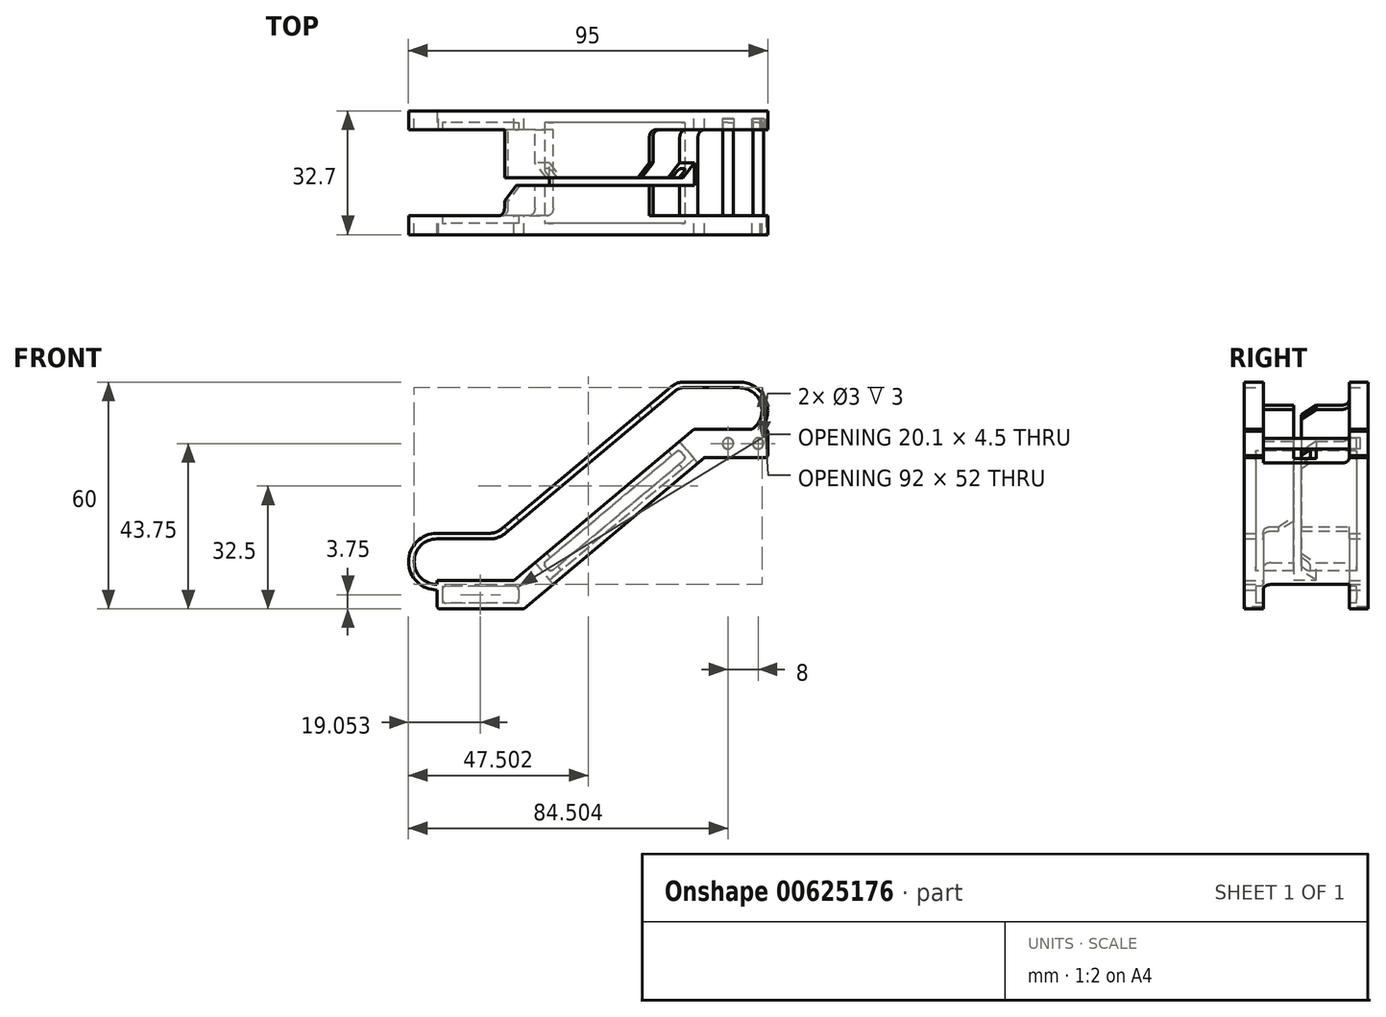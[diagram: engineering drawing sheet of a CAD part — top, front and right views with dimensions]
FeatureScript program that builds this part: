
annotation { "Feature Type Name" : "Feature", "Feature Type Description" : "" }
export const myFeature = defineFeature(function(context is Context, id is Id, definition is map)
    precondition{}
    {
        {
            var Q0;
            Q0=qCreatedBy(makeId("Front.planeOp"),FACE);
            var sketch = newSketch(context, id + "F0", { "sketchPlane" : qUnion([Q0])});
            skLineSegment(sketch, "E0", {"start": v(0, 0) * mm, "end": v(-32.65, 38.92) * mm, "construction": true});
            skLineSegment(sketch, "E1", {"start": v(-32.65, 38.92) * mm, "end": v(25.72, 87.9) * mm, "construction": true});
            skLineSegment(sketch, "E2", {"start": v(25.72, 87.9) * mm, "end": v(58.37, 48.98) * mm, "construction": true});
            skLineSegment(sketch, "E3", {"start": v(58.37, 48.98) * mm, "end": v(0, 0) * mm, "construction": true});
            skLineSegment(sketch, "E4", {"start": v(0, 0) * mm, "end": v(134.97, 0) * mm, "construction": true});
            skLineSegment(sketch, "E5.bottom", {"start": v(8.43, 66.15) * mm, "end": v(19.82, 66.15) * mm, "construction": true});
            skLineSegment(sketch, "E5.top", {"start": v(8.43, 20.9) * mm, "end": v(19.82, 20.9) * mm, "construction": true});
            skLineSegment(sketch, "E5.left", {"start": v(8.43, 66.15) * mm, "end": v(8.43, 20.9) * mm, "construction": true});
            skLineSegment(sketch, "E5.right", {"start": v(19.82, 66.15) * mm, "end": v(19.82, 20.9) * mm, "construction": true});
            skSolve(sketch);
        }
        {
            var Q0;
            Q0=qCreatedBy(makeId("Front.planeOp"),FACE);
            var sketch = newSketch(context, id + "F1", { "sketchPlane" : qUnion([Q0])});
            skLineSegment(sketch, "E6.0", {"start": v(0, 0) * mm, "end": v(134.97, 0) * mm, "construction": true});
            skLineSegment(sketch, "E7.0", {"start": v(58.37, 48.98) * mm, "end": v(0, 0) * mm, "construction": true});
            skLineSegment(sketch, "E8", {"start": v(2.16, 16.17) * mm, "end": v(47.04, 53.83) * mm});
            skLineSegment(sketch, "E9", {"start": v(-1.06, 15) * mm, "end": v(-15.06, 15) * mm});
            skLineSegment(sketch, "E10", {"start": v(50.25, 55) * mm, "end": v(64.94, 55) * mm});
            skLineSegment(sketch, "E11.0", {"start": v(55.71, 40) * mm, "end": v(64.94, 40) * mm});
            skLineSegment(sketch, "E11.1", {"start": v(7.62, 1.17) * mm, "end": v(52.5, 38.83) * mm});
            skLineSegment(sketch, "E11.2", {"start": v(4.4, 0) * mm, "end": v(-15.06, 0) * mm});
            skArc(sketch, "E12", {"start": v(-15.06, 15) * mm, "mid": v(-22.56, 7.5) * mm, "end": v(-15.06, 0) * mm});
            skArc(sketch, "E13", {"start": v(64.94, 55) * mm, "mid": v(72.44, 47.5) * mm, "end": v(64.94, 40) * mm});
            skLineSegment(sketch, "E14", {"start": v(-22.56, 7.5) * mm, "end": v(-22.56, 15.37) * mm, "construction": true});
            skLineSegment(sketch, "E15", {"start": v(72.44, 47.5) * mm, "end": v(72.44, 63.27) * mm, "construction": true});
            skPoint(sketch, "E16.visualSharp", {"position": v(0.76, 15) * mm});
            skArc(sketch, "E16.filletArc", {"start": v(-1.06, 15) * mm, "mid": v(0.65, 15.3) * mm, "end": v(2.16, 16.17) * mm});
            skPoint(sketch, "E17.visualSharp", {"position": v(6.22, 0) * mm});
            skArc(sketch, "E17.filletArc", {"start": v(4.4, 0) * mm, "mid": v(6.11, 0.3) * mm, "end": v(7.62, 1.17) * mm});
            skPoint(sketch, "E18.visualSharp", {"position": v(48.43, 55) * mm});
            skArc(sketch, "E18.filletArc", {"start": v(50.25, 55) * mm, "mid": v(48.54, 54.7) * mm, "end": v(47.04, 53.83) * mm});
            skPoint(sketch, "E19.visualSharp", {"position": v(53.9, 40) * mm});
            skArc(sketch, "E19.filletArc", {"start": v(55.71, 40) * mm, "mid": v(54, 39.7) * mm, "end": v(52.5, 38.83) * mm});
            skLineSegment(sketch, "E20.0", {"start": v(-1.06, 13.5) * mm, "end": v(-15.06, 13.5) * mm});
            skArc(sketch, "E20.1", {"start": v(55.71, 41.5) * mm, "mid": v(53.49, 41.1) * mm, "end": v(51.53, 39.98) * mm});
            skLineSegment(sketch, "E20.2", {"start": v(6.65, 2.32) * mm, "end": v(51.53, 39.98) * mm});
            skArc(sketch, "E20.3", {"start": v(4.4, 1.5) * mm, "mid": v(5.6, 1.71) * mm, "end": v(6.65, 2.32) * mm});
            skLineSegment(sketch, "E20.4", {"start": v(4.4, 1.5) * mm, "end": v(-15.06, 1.5) * mm});
            skLineSegment(sketch, "E20.5", {"start": v(55.71, 41.5) * mm, "end": v(64.94, 41.5) * mm});
            skArc(sketch, "E20.6", {"start": v(-15.06, 13.5) * mm, "mid": v(-21.06, 7.5) * mm, "end": v(-15.06, 1.5) * mm});
            skArc(sketch, "E20.7", {"start": v(64.94, 53.5) * mm, "mid": v(70.94, 47.5) * mm, "end": v(64.94, 41.5) * mm});
            skLineSegment(sketch, "E20.8", {"start": v(50.25, 53.5) * mm, "end": v(64.94, 53.5) * mm});
            skArc(sketch, "E20.9", {"start": v(50.25, 53.5) * mm, "mid": v(49.06, 53.29) * mm, "end": v(48, 52.68) * mm});
            skLineSegment(sketch, "E20.10", {"start": v(3.12, 15.02) * mm, "end": v(48, 52.68) * mm});
            skArc(sketch, "E20.11", {"start": v(-1.06, 13.5) * mm, "mid": v(1.17, 13.9) * mm, "end": v(3.12, 15.02) * mm});
            skSolve(sketch);
        }
        {
            var Q0;
            Q0 = qSketchRegion(id + "F1", true);
            extrude(context, id + "F2", {"entities" : qUnion([Q0]), "endBound" : BoundingType.SYMMETRIC, "depth" : 32.7 * mm, "offsetDistance" : 25 * mm});
        }
        {
            var Q0;
            Q0=qCreatedBy(makeId("Front.planeOp"),FACE);
            var sketch = newSketch(context, id + "F3", { "sketchPlane" : qUnion([Q0])});
            skLineSegment(sketch, "E21.0", {"start": v(0, 0) * mm, "end": v(134.97, 0) * mm, "construction": true});
            skLineSegment(sketch, "E22.0", {"start": v(58.37, 48.98) * mm, "end": v(0, 0) * mm, "construction": true});
            skLineSegment(sketch, "E23.0", {"start": v(7.62, 1.17) * mm, "end": v(52.5, 38.83) * mm, "construction": true});
            skLineSegment(sketch, "E24", {"start": v(53.9, 40) * mm, "end": v(6.22, 0) * mm});
            skLineSegment(sketch, "E25", {"start": v(6.22, 0) * mm, "end": v(-15.06, 0) * mm});
            skLineSegment(sketch, "E26.0", {"start": v(55.71, 40) * mm, "end": v(64.94, 40) * mm, "construction": true});
            skLineSegment(sketch, "E27", {"start": v(53.9, 40) * mm, "end": v(72.44, 40) * mm});
            skLineSegment(sketch, "E28.0", {"start": v(5.31, 2.5) * mm, "end": v(-15.06, 2.5) * mm});
            skLineSegment(sketch, "E28.1", {"start": v(52.98, 42.5) * mm, "end": v(5.31, 2.5) * mm});
            skLineSegment(sketch, "E28.2", {"start": v(52.98, 42.5) * mm, "end": v(72.44, 42.5) * mm});
            skLineSegment(sketch, "E29", {"start": v(-15.06, 0) * mm, "end": v(-15.06, 2.5) * mm});
            skLineSegment(sketch, "E30", {"start": v(72.44, 42.5) * mm, "end": v(72.44, 40) * mm});
            skLineSegment(sketch, "E31", {"start": v(52.5, 38.83) * mm, "end": v(72.44, 38.83) * mm});
            skLineSegment(sketch, "E32", {"start": v(72.44, 38.83) * mm, "end": v(72.44, 40) * mm});
            skLineSegment(sketch, "E33.0", {"start": v(8.04, -5) * mm, "end": v(-15.06, -5) * mm});
            skLineSegment(sketch, "E33.1", {"start": v(55.71, 35) * mm, "end": v(8.04, -5) * mm});
            skLineSegment(sketch, "E33.2", {"start": v(55.71, 35) * mm, "end": v(72.44, 35) * mm});
            skLineSegment(sketch, "E34", {"start": v(-15.06, -5) * mm, "end": v(-15.06, 0) * mm});
            skLineSegment(sketch, "E35", {"start": v(72.44, 35) * mm, "end": v(72.44, 38.83) * mm});
            skLineSegment(sketch, "E36", {"start": v(-25.44, 35.18) * mm, "end": v(32.93, 84.16) * mm, "construction": true});
            skLineSegment(sketch, "E37", {"start": v(32.93, 84.16) * mm, "end": v(65.59, 45.24) * mm, "construction": true});
            skLineSegment(sketch, "E38", {"start": v(65.59, 45.24) * mm, "end": v(7.22, -3.74) * mm, "construction": true});
            skLineSegment(sketch, "E39", {"start": v(7.22, -3.74) * mm, "end": v(-25.44, 35.18) * mm, "construction": true});
            skLineSegment(sketch, "E40.bottom", {"start": v(36.03, 62.16) * mm, "end": v(44.03, 62.16) * mm, "construction": true});
            skLineSegment(sketch, "E40.top", {"start": v(36.03, 27.16) * mm, "end": v(44.03, 27.16) * mm, "construction": true});
            skLineSegment(sketch, "E40.left", {"start": v(36.03, 62.16) * mm, "end": v(36.03, 27.16) * mm, "construction": true});
            skLineSegment(sketch, "E40.right", {"start": v(44.03, 62.16) * mm, "end": v(44.03, 27.16) * mm, "construction": true});
            skSolve(sketch);
        }
        {
            var Q0;
            Q0 = qSketchRegion(id + "F3", true);
            extrude(context, id + "F4", {"entities" : qUnion([Q0]), "operationType" : NewBodyOperationType.ADD, "endBound" : BoundingType.SYMMETRIC, "depth" : 32.7 * mm, "offsetDistance" : 25 * mm});
        }
        {
            var Q0;
            Q0=qCreatedBy(makeId("Front.planeOp"),FACE);
            var sketch = newSketch(context, id + "F5", { "sketchPlane" : qUnion([Q0])});
            skLineSegment(sketch, "E41.bottom", {"start": v(-30.59, 62.87) * mm, "end": v(81.8, 62.87) * mm});
            skLineSegment(sketch, "E41.top", {"start": v(-30.59, -9.09) * mm, "end": v(81.8, -9.09) * mm});
            skLineSegment(sketch, "E41.left", {"start": v(-30.59, 62.87) * mm, "end": v(-30.59, -9.09) * mm});
            skLineSegment(sketch, "E41.right", {"start": v(81.8, 62.87) * mm, "end": v(81.8, -9.09) * mm});
            skSolve(sketch);
        }
        {
            var Q0;
            Q0 = qSketchRegion(id + "F5", true);
            extrude(context, id + "F6", {"entities" : qUnion([Q0]), "operationType" : NewBodyOperationType.REMOVE, "endBound" : BoundingType.SYMMETRIC, "oppositeDirection" : true, "depth" : 22.7 * mm, "offsetDistance" : 25 * mm});
        }
        {
            var Q0;
            Q0=qCreatedBy(makeId("Front.planeOp"),FACE);
            var sketch = newSketch(context, id + "F7", { "sketchPlane" : qUnion([Q0])});
            skLineSegment(sketch, "E42.0", {"start": v(52.98, 42.5) * mm, "end": v(5.31, 2.5) * mm, "construction": true});
            skLineSegment(sketch, "E43.0", {"start": v(55.71, 35) * mm, "end": v(8.04, -5) * mm, "construction": true});
            skLineSegment(sketch, "E44", {"start": v(10.88, 7.17) * mm, "end": v(15.7, 1.43) * mm});
            skLineSegment(sketch, "E45", {"start": v(15.7, 1.43) * mm, "end": v(54, 33.57) * mm});
            skLineSegment(sketch, "E46", {"start": v(54, 33.57) * mm, "end": v(49.18, 39.31) * mm});
            skLineSegment(sketch, "E47", {"start": v(49.18, 39.31) * mm, "end": v(10.88, 7.17) * mm});
            skLineSegment(sketch, "E48.0", {"start": v(2.85, 16.75) * mm, "end": v(41.15, 48.89) * mm});
            skLineSegment(sketch, "E49.0", {"start": v(3.81, 15.6) * mm, "end": v(42.11, 47.74) * mm});
            skLineSegment(sketch, "E50", {"start": v(3.81, 15.6) * mm, "end": v(2.85, 16.75) * mm});
            skLineSegment(sketch, "E51", {"start": v(42.11, 47.74) * mm, "end": v(41.15, 48.89) * mm});
            skPoint(sketch, "E52.orphan", {"position": v(3.12, 15.02) * mm});
            skPoint(sketch, "E53.orphan", {"position": v(2.16, 16.17) * mm});
            skPoint(sketch, "E54.orphan", {"position": v(48, 52.68) * mm});
            skPoint(sketch, "E55.orphan", {"position": v(47.04, 53.83) * mm});
            skSolve(sketch);
        }
        {
            var Q0;
            Q0 = qSketchRegion(id + "F7", true);
            var Q1;
            Q1=makeQuery(id+"F6.boolean.opBoolean","COPY",FACE,{"derivedFrom":makeQuery(id+"F6.opExtrude","CAP_FACE",FACE,{"disambiguationData":[OSD([sQuery(id+"F5.wireOp",EDGE,"E41.bottom"),sQuery(id+"F5.wireOp",EDGE,"E41.top"),sQuery(id+"F5.wireOp",EDGE,"E41.left"),sQuery(id+"F5.wireOp",EDGE,"E41.right")])],"isStart":true})});
            var Q2;
            Q2=makeQuery(id+"F6.boolean.opBoolean","COPY",FACE,{"derivedFrom":makeQuery(id+"F6.opExtrude","CAP_FACE",FACE,{"disambiguationData":[OSD([sQuery(id+"F5.wireOp",EDGE,"E41.bottom"),sQuery(id+"F5.wireOp",EDGE,"E41.top"),sQuery(id+"F5.wireOp",EDGE,"E41.left"),sQuery(id+"F5.wireOp",EDGE,"E41.right")])],"isStart":false})});
            extrude(context, id + "F8", {"entities" : qUnion([Q0]), "operationType" : NewBodyOperationType.ADD, "endBound" : BoundingType.UP_TO_SURFACE, "depth" : 25 * mm, "endBoundEntityFace" : qUnion([Q1]), "offsetDistance" : 25 * mm, "hasSecondDirection" : true, "secondDirectionBound" : SecondDirectionBoundingType.UP_TO_SURFACE, "secondDirectionOppositeDirection" : true, "secondDirectionDepth" : 25 * mm, "secondDirectionBoundEntityFace" : qUnion([Q2])});
        }
        {
            var Q0;
            Q0=makeQuery(id+"F8.opExtrude","SWEPT_FACE",FACE,{"disambiguationData":[OSD([sQuery(id+"F7.wireOp",EDGE,"E44")])]});
            var sketch = newSketch(context, id + "F9", { "sketchPlane" : qUnion([Q0])});
            skLineSegment(sketch, "E56", {"start": v(0, -1.5) * mm, "end": v(0, 13.32) * mm, "construction": true});
            skLineSegment(sketch, "E57.bottom", {"start": v(1.35, -1.5) * mm, "end": v(3.35, -1.5) * mm});
            skLineSegment(sketch, "E57.top", {"start": v(1.35, -9) * mm, "end": v(3.35, -9) * mm});
            skLineSegment(sketch, "E57.left", {"start": v(1.35, -1.5) * mm, "end": v(1.35, -9) * mm});
            skLineSegment(sketch, "E57.right", {"start": v(3.35, -1.5) * mm, "end": v(3.35, -9) * mm});
            skLineSegment(sketch, "E58", {"start": v(-3, -9) * mm, "end": v(-3, -7.5) * mm});
            skLineSegment(sketch, "E59", {"start": v(-3, -7.5) * mm, "end": v(1.35, -7.5) * mm});
            skLineSegment(sketch, "E60", {"start": v(-3, -9) * mm, "end": v(1.35, -9) * mm});
            skLineSegment(sketch, "E61", {"start": v(2.35, -1.5) * mm, "end": v(2.35, -9) * mm, "construction": true});
            skLineSegment(sketch, "E62.0", {"start": v(11.35, 11) * mm, "end": v(-11.35, 11) * mm, "construction": true});
            skLineSegment(sketch, "E63.0", {"start": v(11.35, 9.5) * mm, "end": v(-11.35, 9.5) * mm, "construction": true});
            skLineSegment(sketch, "E64.bottom", {"start": v(1.35, 11) * mm, "end": v(3.35, 11) * mm});
            skLineSegment(sketch, "E64.top", {"start": v(1.35, 9.5) * mm, "end": v(3.35, 9.5) * mm});
            skLineSegment(sketch, "E64.left", {"start": v(1.35, 11) * mm, "end": v(1.35, 9.5) * mm});
            skLineSegment(sketch, "E64.right", {"start": v(3.35, 11) * mm, "end": v(3.35, 9.5) * mm});
            skSolve(sketch);
        }
        {
            var Q0;
            Q0 = qSketchRegion(id + "F9", true);
            var Q1;
            Q1=makeQuery(id+"F8.opExtrude","SWEPT_FACE",FACE,{"disambiguationData":[OSD([sQuery(id+"F7.wireOp",EDGE,"E46")])]});
            extrude(context, id + "F10", {"entities" : qUnion([Q0]), "operationType" : NewBodyOperationType.REMOVE, "endBound" : BoundingType.UP_TO_SURFACE, "oppositeDirection" : true, "depth" : 63.9 * mm, "endBoundEntityFace" : qUnion([Q1]), "offsetDistance" : 25 * mm});
        }
        {
            var Q0;
            Q0=makeQuery(id+"F10.boolean.opBoolean","SPLIT",FACE,{"disambiguationData":[TD([makeQuery(id+"F10.opExtrude","SWEPT_FACE",FACE,{"disambiguationData":[OSD([sQuery(id+"F9.wireOp",EDGE,"E57.right")])]})])],"derivedFrom":makeQuery(id+"F8.opExtrude","SWEPT_FACE",FACE,{"disambiguationData":[OSD([sQuery(id+"F7.wireOp",EDGE,"E44")])]})});
            var sketch = newSketch(context, id + "F11", { "sketchPlane" : qUnion([Q0])});
            skLineSegment(sketch, "E65.bottom", {"start": v(3.35, -9) * mm, "end": v(-3, -9) * mm});
            skLineSegment(sketch, "E65.top", {"start": v(3.35, -7.5) * mm, "end": v(-3, -7.5) * mm});
            skLineSegment(sketch, "E65.left", {"start": v(3.35, -9) * mm, "end": v(3.35, -7.5) * mm});
            skLineSegment(sketch, "E65.right", {"start": v(-3, -9) * mm, "end": v(-3, -7.5) * mm});
            skLineSegment(sketch, "E66.0", {"start": v(-3, -7.5) * mm, "end": v(1.35, -7.5) * mm, "construction": true});
            skSolve(sketch);
        }
        {
            var Q0;
            Q0 = qSketchRegion(id + "F11", true);
            var Q1;
            Q1=makeQuery(id+"F10.boolean.opBoolean","SPLIT",FACE,{"disambiguationData":[TD([makeQuery(id+"F10.opExtrude","SWEPT_FACE",FACE,{"disambiguationData":[OSD([sQuery(id+"F9.wireOp",EDGE,"E57.right")])]})])],"derivedFrom":makeQuery(id+"F8.opExtrude","SWEPT_FACE",FACE,{"disambiguationData":[OSD([sQuery(id+"F7.wireOp",EDGE,"E46")])]})});
            extrude(context, id + "F12", {"entities" : qUnion([Q0]), "operationType" : NewBodyOperationType.ADD, "endBound" : BoundingType.UP_TO_SURFACE, "oppositeDirection" : true, "depth" : 53.4 * mm, "endBoundEntityFace" : qUnion([Q1]), "offsetDistance" : 25 * mm});
        }
        {
            var Q0;
            Q0=makeQuery(id+"F8.opExtrude","CAP_EDGE",EDGE,{"disambiguationData":[OSD([sQuery(id+"F7.wireOp",EDGE,"E44")])],"isStart":true});
            var Q1;
            Q1=makeQuery(id+"F8.opExtrude","CAP_EDGE",EDGE,{"disambiguationData":[OSD([sQuery(id+"F7.wireOp",EDGE,"E44")])],"isStart":false});
            var Q2;
            Q2=makeQuery(id+"F8.opExtrude","CAP_EDGE",EDGE,{"disambiguationData":[OSD([sQuery(id+"F7.wireOp",EDGE,"E46")])],"isStart":true});
            var Q3;
            Q3=makeQuery(id+"F8.opExtrude","CAP_EDGE",EDGE,{"disambiguationData":[OSD([sQuery(id+"F7.wireOp",EDGE,"E46")])],"isStart":false});
            var Q4;
            Q4=makeQuery(id+"F8.opExtrude","CAP_EDGE",EDGE,{"disambiguationData":[OSD([sQuery(id+"F7.wireOp",EDGE,"E50")])],"isStart":true});
            var Q5;
            Q5=makeQuery(id+"F8.opExtrude","CAP_EDGE",EDGE,{"disambiguationData":[OSD([sQuery(id+"F7.wireOp",EDGE,"E50")])],"isStart":false});
            var Q6;
            Q6=makeQuery(id+"F8.opExtrude","CAP_EDGE",EDGE,{"disambiguationData":[OSD([sQuery(id+"F7.wireOp",EDGE,"E51")])],"isStart":true});
            var Q7;
            Q7=makeQuery(id+"F8.opExtrude","CAP_EDGE",EDGE,{"disambiguationData":[OSD([sQuery(id+"F7.wireOp",EDGE,"E51")])],"isStart":false});
            fillet(context, id + "F13", {"entities" : qUnion([Q0, Q1, Q2, Q3, Q4, Q5, Q6, Q7]), "radius" : 2 * mm, "tangentPropagation" : true, "allowEdgeOverflow" : false});
        }
        {
            var Q0;
            Q0=qCreatedBy(makeId("Front.planeOp"),FACE);
            var sketch = newSketch(context, id + "F14", { "sketchPlane" : qUnion([Q0])});
            skLineSegment(sketch, "E67.0", {"start": v(72.44, 42.5) * mm, "end": v(72.44, 35) * mm, "construction": true});
            skLineSegment(sketch, "E68", {"start": v(72.44, 38.75) * mm, "end": v(40.1, 38.75) * mm, "construction": true});
            skCircle(sketch, "E69", {"center": v(69.94, 38.75) * mm, "radius": 1.5 * mm});
            skCircle(sketch, "E70", {"center": v(61.94, 38.75) * mm, "radius": 1.5 * mm});
            skSolve(sketch);
        }
        {
            var Q0;
            Q0 = qSketchRegion(id + "F14", true);
            extrude(context, id + "F15", {"entities" : qUnion([Q0]), "operationType" : NewBodyOperationType.REMOVE, "oppositeDirection" : true, "depth" : 14.35 * mm, "offsetDistance" : 25 * mm});
        }
        {
            var Q0;
            Q0=makeQuery(id+"F6.boolean.opBoolean","COPY",FACE,{"derivedFrom":makeQuery(id+"F6.opExtrude","CAP_FACE",FACE,{"disambiguationData":[OSD([sQuery(id+"F5.wireOp",EDGE,"E41.bottom"),sQuery(id+"F5.wireOp",EDGE,"E41.top"),sQuery(id+"F5.wireOp",EDGE,"E41.left"),sQuery(id+"F5.wireOp",EDGE,"E41.right")])],"isStart":true})});
            var sketch = newSketch(context, id + "F16", { "sketchPlane" : qUnion([Q0])});
            skCircle(sketch, "E71.0", {"center": v(-69.94, 38.75) * mm, "radius": 1.5 * mm, "construction": true});
            skCircle(sketch, "E72.0", {"center": v(-61.94, 38.75) * mm, "radius": 1.5 * mm, "construction": true});
            skCircle(sketch, "E73", {"center": v(-69.94, 38.75) * mm, "radius": 1.4 * mm});
            skCircle(sketch, "E74", {"center": v(-61.94, 38.75) * mm, "radius": 1.4 * mm});
            skSolve(sketch);
        }
        {
            var Q0;
            Q0 = qSketchRegion(id + "F16", true);
            extrude(context, id + "F17", {"entities" : qUnion([Q0]), "operationType" : NewBodyOperationType.ADD, "depth" : 24.7 * mm, "offsetDistance" : 25 * mm});
        }
        {
            var Q0;
            Q0=makeQuery(id+"F17.opExtrude","CAP_EDGE",EDGE,{"disambiguationData":[OSD([sQuery(id+"F16.wireOp",EDGE,"E71.0")])],"isStart":true});
            var Q1;
            Q1=makeQuery(id+"F17.opExtrude","CAP_EDGE",EDGE,{"disambiguationData":[OSD([sQuery(id+"F16.wireOp",EDGE,"E72.0")])],"isStart":true});
            var Q2;
            {var subQ0=sQuery(id+"F3.wireOp",EDGE,"E34");var subQ2=sQuery(id+"F3.wireOp",EDGE,"E33.0");Q2=makeQuery(id+"F6.boolean.opBoolean","SPLIT",EDGE,{"disambiguationData":[TD([makeQuery(id+"F6.opExtrude","CAP_FACE",FACE,{"disambiguationData":[OSD([sQuery(id+"F5.wireOp",EDGE,"E41.bottom"),sQuery(id+"F5.wireOp",EDGE,"E41.top"),sQuery(id+"F5.wireOp",EDGE,"E41.left"),sQuery(id+"F5.wireOp",EDGE,"E41.right")])],"isStart":true})])],"derivedFrom":makeQuery(id+"F4.opExtrude","SWEPT_EDGE",EDGE,{"disambiguationData":[OSD([subQ2,subQ0])]})});}
            var Q3;
            {var subQ0=sQuery(id+"F3.wireOp",EDGE,"E33.0");var subQ1=sQuery(id+"F3.wireOp",EDGE,"E34");Q3=makeQuery(id+"F6.boolean.opBoolean","SPLIT",EDGE,{"disambiguationData":[TD([makeQuery(id+"F6.opExtrude","CAP_FACE",FACE,{"disambiguationData":[OSD([sQuery(id+"F5.wireOp",EDGE,"E41.bottom"),sQuery(id+"F5.wireOp",EDGE,"E41.top"),sQuery(id+"F5.wireOp",EDGE,"E41.left"),sQuery(id+"F5.wireOp",EDGE,"E41.right")])],"isStart":false})])],"derivedFrom":makeQuery(id+"F4.opExtrude","SWEPT_EDGE",EDGE,{"disambiguationData":[OSD([subQ0,subQ1])]})});}
            var Q4;
            {var subQ0=sQuery(id+"F3.wireOp",EDGE,"E35");var subQ3=sQuery(id+"F3.wireOp",EDGE,"E33.2");Q4=makeQuery(id+"F6.boolean.opBoolean","SPLIT",EDGE,{"disambiguationData":[TD([makeQuery(id+"F6.opExtrude","CAP_FACE",FACE,{"disambiguationData":[OSD([sQuery(id+"F5.wireOp",EDGE,"E41.bottom"),sQuery(id+"F5.wireOp",EDGE,"E41.top"),sQuery(id+"F5.wireOp",EDGE,"E41.left"),sQuery(id+"F5.wireOp",EDGE,"E41.right")])],"isStart":true})])],"derivedFrom":makeQuery(id+"F4.opExtrude","SWEPT_EDGE",EDGE,{"disambiguationData":[OSD([subQ3,subQ0])]})});}
            var Q5;
            {var subQ0=sQuery(id+"F3.wireOp",EDGE,"E33.2");var subQ1=sQuery(id+"F3.wireOp",EDGE,"E35");Q5=makeQuery(id+"F6.boolean.opBoolean","SPLIT",EDGE,{"disambiguationData":[TD([makeQuery(id+"F6.opExtrude","CAP_FACE",FACE,{"disambiguationData":[OSD([sQuery(id+"F5.wireOp",EDGE,"E41.bottom"),sQuery(id+"F5.wireOp",EDGE,"E41.top"),sQuery(id+"F5.wireOp",EDGE,"E41.left"),sQuery(id+"F5.wireOp",EDGE,"E41.right")])],"isStart":false})])],"derivedFrom":makeQuery(id+"F4.opExtrude","SWEPT_EDGE",EDGE,{"disambiguationData":[OSD([subQ0,subQ1])]})});}
            var Q6;
            {var subQ2=sQuery(id+"F3.wireOp",EDGE,"E30");var subQ3=sQuery(id+"F3.wireOp",EDGE,"E28.2");Q6=makeQuery(id+"F6.boolean.opBoolean","SPLIT",EDGE,{"disambiguationData":[TD([makeQuery(id+"F6.opExtrude","CAP_FACE",FACE,{"disambiguationData":[OSD([sQuery(id+"F5.wireOp",EDGE,"E41.bottom"),sQuery(id+"F5.wireOp",EDGE,"E41.top"),sQuery(id+"F5.wireOp",EDGE,"E41.left"),sQuery(id+"F5.wireOp",EDGE,"E41.right")])],"isStart":true})])],"derivedFrom":makeQuery(id+"F4.opExtrude","SWEPT_EDGE",EDGE,{"disambiguationData":[OSD([subQ3,subQ2])]})});}
            var Q7;
            {var subQ0=sQuery(id+"F3.wireOp",EDGE,"E28.2");var subQ3=sQuery(id+"F3.wireOp",EDGE,"E30");Q7=makeQuery(id+"F6.boolean.opBoolean","SPLIT",EDGE,{"disambiguationData":[TD([makeQuery(id+"F6.opExtrude","CAP_FACE",FACE,{"disambiguationData":[OSD([sQuery(id+"F5.wireOp",EDGE,"E41.bottom"),sQuery(id+"F5.wireOp",EDGE,"E41.top"),sQuery(id+"F5.wireOp",EDGE,"E41.left"),sQuery(id+"F5.wireOp",EDGE,"E41.right")])],"isStart":false})])],"derivedFrom":makeQuery(id+"F4.opExtrude","SWEPT_EDGE",EDGE,{"disambiguationData":[OSD([subQ0,subQ3])]})});}
            var Q8;
            Q8=makeQuery(id+"F17.opExtrude","CAP_EDGE",EDGE,{"disambiguationData":[OSD([sQuery(id+"F16.wireOp",EDGE,"E73")])],"isStart":true});
            var Q9;
            Q9=makeQuery(id+"F17.opExtrude","CAP_EDGE",EDGE,{"disambiguationData":[OSD([sQuery(id+"F16.wireOp",EDGE,"E74")])],"isStart":true});
            chamfer(context, id + "F18", {"entities" : qUnion([Q0, Q1, Q2, Q3, Q4, Q5, Q6, Q7, Q8, Q9]), "width" : .5 * mm, "tangentPropagation" : true});
        }
        {
            var Q0;
            Q0=qCreatedBy(makeId("Front.planeOp"),FACE);
            var sketch = newSketch(context, id + "F19", { "sketchPlane" : qUnion([Q0])});
            skLineSegment(sketch, "E75.0", {"start": v(14.74, 2.58) * mm, "end": v(10.88, 7.17) * mm, "construction": true});
            skLineSegment(sketch, "E76.0", {"start": v(49.18, 39.31) * mm, "end": v(53.04, 34.72) * mm, "construction": true});
            skLineSegment(sketch, "E77.0", {"start": v(53.04, 34.72) * mm, "end": v(14.74, 2.58) * mm, "construction": true});
            skLineSegment(sketch, "E78.0", {"start": v(49.18, 39.31) * mm, "end": v(10.88, 7.17) * mm, "construction": true});
            skPoint(sketch, "E79.orphan", {"position": v(5.31, 2.5) * mm});
            skPoint(sketch, "E80.orphan", {"position": v(15.7, 1.43) * mm});
            skPoint(sketch, "E81.orphan", {"position": v(54, 33.57) * mm});
            skPoint(sketch, "E82.orphan", {"position": v(52.98, 42.5) * mm});
            skLineSegment(sketch, "E83.0", {"start": v(48.23, 36.56) * mm, "end": v(13.76, 7.63) * mm});
            skLineSegment(sketch, "E83.1", {"start": v(49.64, 36.43) * mm, "end": v(50.29, 35.67) * mm});
            skLineSegment(sketch, "E83.2", {"start": v(50.16, 34.26) * mm, "end": v(15.69, 5.33) * mm});
            skLineSegment(sketch, "E83.3", {"start": v(14.28, 5.46) * mm, "end": v(13.64, 6.22) * mm});
            skPoint(sketch, "E84.visualSharp", {"position": v(13, 6.99) * mm});
            skArc(sketch, "E84.filletArc", {"start": v(13.76, 7.63) * mm, "mid": v(13.4, 6.95) * mm, "end": v(13.64, 6.22) * mm});
            skPoint(sketch, "E85.visualSharp", {"position": v(14.92, 4.7) * mm});
            skArc(sketch, "E85.filletArc", {"start": v(14.28, 5.46) * mm, "mid": v(14.96, 5.1) * mm, "end": v(15.69, 5.33) * mm});
            skPoint(sketch, "E86.visualSharp", {"position": v(50.93, 34.9) * mm});
            skArc(sketch, "E86.filletArc", {"start": v(50.16, 34.26) * mm, "mid": v(50.52, 34.94) * mm, "end": v(50.29, 35.67) * mm});
            skPoint(sketch, "E87.visualSharp", {"position": v(49, 37.2) * mm});
            skArc(sketch, "E87.filletArc", {"start": v(49.64, 36.43) * mm, "mid": v(48.96, 36.79) * mm, "end": v(48.23, 36.56) * mm});
            skLineSegment(sketch, "E88.bottom", {"start": v(5.54, 1) * mm, "end": v(-12.56, 1) * mm});
            skLineSegment(sketch, "E88.top", {"start": v(5.54, -3.5) * mm, "end": v(-12.56, -3.5) * mm});
            skLineSegment(sketch, "E88.left", {"start": v(6.54, 0) * mm, "end": v(6.54, -2.5) * mm});
            skLineSegment(sketch, "E88.right", {"start": v(-13.56, 0) * mm, "end": v(-13.56, -2.5) * mm});
            skPoint(sketch, "E89.visualSharp", {"position": v(6.54, 1) * mm});
            skArc(sketch, "E89.filletArc", {"start": v(6.54, 0) * mm, "mid": v(6.25, 0.7) * mm, "end": v(5.54, 1) * mm});
            skPoint(sketch, "E90.visualSharp", {"position": v(6.54, -3.5) * mm});
            skArc(sketch, "E90.filletArc", {"start": v(5.54, -3.5) * mm, "mid": v(6.25, -3.2) * mm, "end": v(6.54, -2.5) * mm});
            skPoint(sketch, "E91.visualSharp", {"position": v(-13.56, -3.5) * mm});
            skArc(sketch, "E91.filletArc", {"start": v(-13.56, -2.5) * mm, "mid": v(-13.26, -3.2) * mm, "end": v(-12.56, -3.5) * mm});
            skPoint(sketch, "E92.visualSharp", {"position": v(-13.56, 1) * mm});
            skArc(sketch, "E92.filletArc", {"start": v(-12.56, 1) * mm, "mid": v(-13.26, 0.7) * mm, "end": v(-13.56, 0) * mm});
            skSolve(sketch);
        }
        {
            var Q0;
            Q0 = qSketchRegion(id + "F19", true);
            extrude(context, id + "F20", {"entities" : qUnion([Q0]), "operationType" : NewBodyOperationType.REMOVE, "endBound" : BoundingType.SYMMETRIC, "oppositeDirection" : true, "depth" : 26.7 * mm, "offsetDistance" : 25 * mm});
        }
        {
            var Q0;
            Q0=makeQuery(id+"F10.boolean.opBoolean","COPY",EDGE,{"derivedFrom":makeQuery(id+"F10.opExtrude","CAP_EDGE",EDGE,{"disambiguationData":[OSD([sQuery(id+"F9.wireOp",EDGE,"E57.left")])],"isStart":true})});
            var Q1;
            Q1=makeQuery(id+"F10.boolean.opBoolean","COPY",EDGE,{"derivedFrom":makeQuery(id+"F10.opExtrude","CAP_EDGE",EDGE,{"disambiguationData":[OSD([sQuery(id+"F9.wireOp",EDGE,"E57.right")])],"isStart":true})});
            var Q2;
            Q2=makeQuery(id+"F10.boolean.opBoolean","COPY",EDGE,{"derivedFrom":makeQuery(id+"F10.opExtrude","CAP_EDGE",EDGE,{"disambiguationData":[OSD([sQuery(id+"F9.wireOp",EDGE,"E64.right")])],"isStart":true})});
            var Q3;
            Q3=makeQuery(id+"F10.boolean.opBoolean","COPY",EDGE,{"derivedFrom":makeQuery(id+"F10.opExtrude","CAP_EDGE",EDGE,{"disambiguationData":[OSD([sQuery(id+"F9.wireOp",EDGE,"E64.left")])],"isStart":true})});
            var Q4;
            Q4=makeQuery(id+"F10.boolean.opBoolean","COPY",EDGE,{"derivedFrom":makeQuery(id+"F10.opExtrude","CAP_EDGE",EDGE,{"disambiguationData":[OSD([sQuery(id+"F9.wireOp",EDGE,"E64.left")])],"isStart":false})});
            var Q5;
            Q5=makeQuery(id+"F10.boolean.opBoolean","COPY",EDGE,{"derivedFrom":makeQuery(id+"F10.opExtrude","CAP_EDGE",EDGE,{"disambiguationData":[OSD([sQuery(id+"F9.wireOp",EDGE,"E64.right")])],"isStart":false})});
            var Q6;
            Q6=makeQuery(id+"F10.boolean.opBoolean","COPY",EDGE,{"derivedFrom":makeQuery(id+"F10.opExtrude","CAP_EDGE",EDGE,{"disambiguationData":[OSD([sQuery(id+"F9.wireOp",EDGE,"E57.left")])],"isStart":false})});
            var Q7;
            Q7=makeQuery(id+"F10.boolean.opBoolean","COPY",EDGE,{"derivedFrom":makeQuery(id+"F10.opExtrude","CAP_EDGE",EDGE,{"disambiguationData":[OSD([sQuery(id+"F9.wireOp",EDGE,"E57.right")])],"isStart":false})});
            chamfer(context, id + "F21", {"entities" : qUnion([Q0, Q1, Q2, Q3, Q4, Q5, Q6, Q7]), "width" : 4 * mm, "tangentPropagation" : true});
        }
    });
